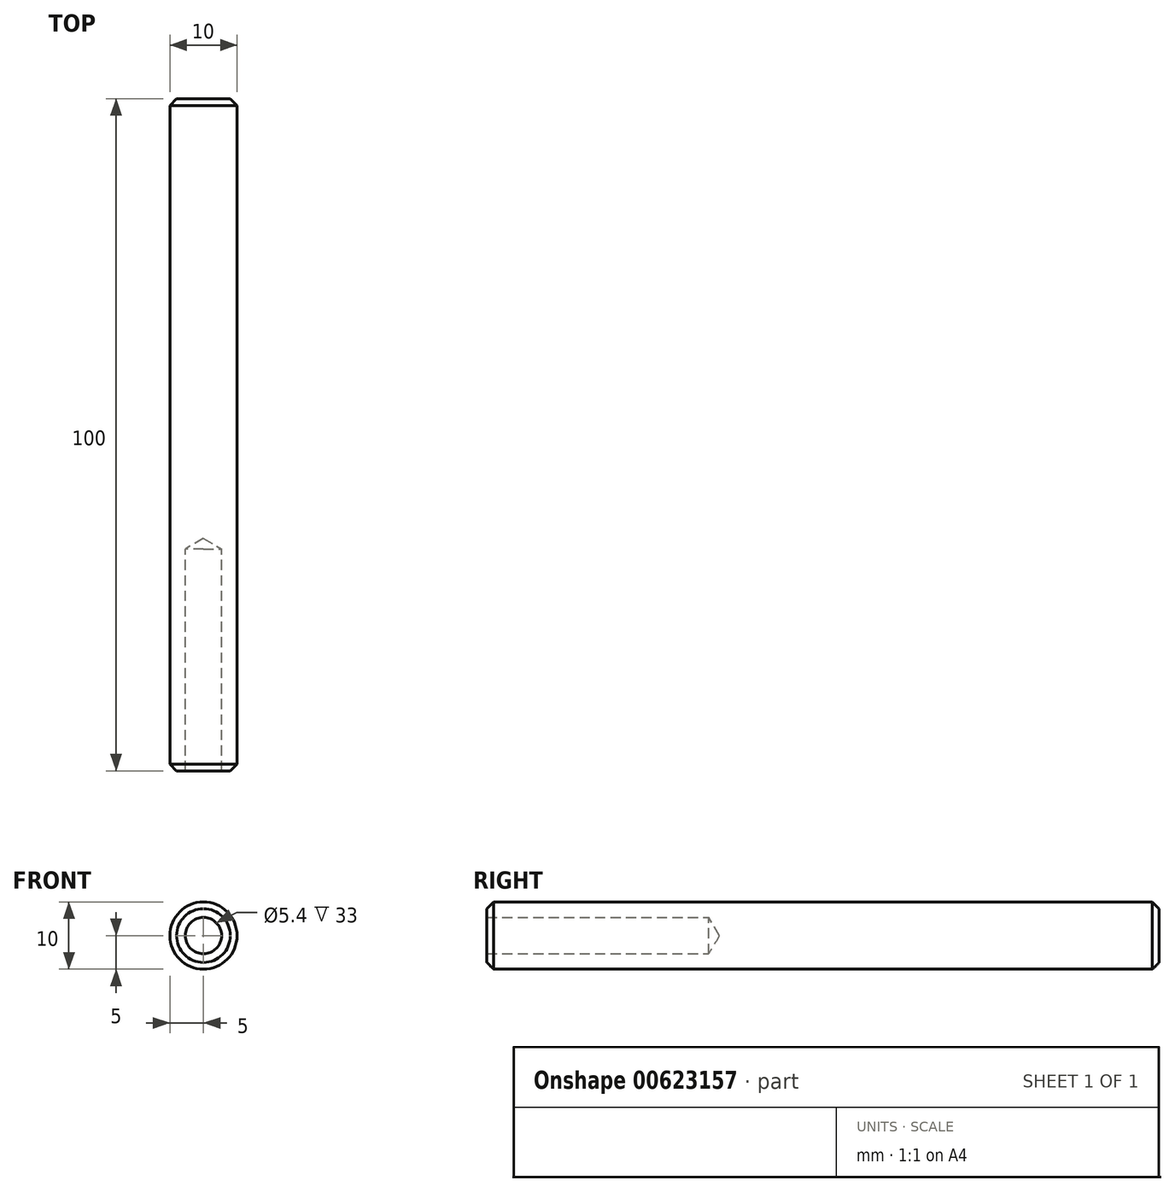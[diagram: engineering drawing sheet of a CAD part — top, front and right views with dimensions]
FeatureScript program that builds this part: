
annotation { "Feature Type Name" : "Feature", "Feature Type Description" : "" }
export const myFeature = defineFeature(function(context is Context, id is Id, definition is map)
    precondition{}
    {
        {
            var Q0;
            Q0=qCreatedBy(makeId("Front.planeOp"),FACE);
            var sketch = newSketch(context, id + "F0", { "sketchPlane" : qUnion([Q0])});
            skCircle(sketch, "E0", {"center": v(0, 0) * mm, "radius": 5 * mm});
            skSolve(sketch);
        }
        {
            var Q0;
            Q0=qSketchRegion(id+"F0",true);
            extrude(context, id + "F1", {"entities" : qUnion([Q0]), "offsetDistance" : 25 * mm, "depth" : 100 * mm});
        }
        {
            var Q0;
            Q0=makeQuery(id+"F1.opExtrude","CAP_EDGE",EDGE,{"disambiguationData":[OSD([sQuery(id+"F0.wireOp",EDGE,"E0")])],"isStart":false});
            var Q1;
            Q1=makeQuery(id+"F1.opExtrude","CAP_EDGE",EDGE,{"disambiguationData":[OSD([sQuery(id+"F0.wireOp",EDGE,"E0")])],"isStart":true});
            chamfer(context, id + "F2", {"entities" : qUnion([Q0, Q1]), "width" : 1 * mm, "tangentPropagation" : true});
        }
        {
            var Q0;
            Q0=makeQuery(id+"F1.opExtrude","CAP_FACE",FACE,{"disambiguationData":[OSD([sQuery(id+"F0.wireOp",EDGE,"E0")])],"isStart":false});
            var sketch = newSketch(context, id + "F3", { "sketchPlane" : qUnion([Q0])});
            skPoint(sketch, "E1", {"position": v(0, 0) * mm});
            skSolve(sketch);
        }
        {
            var Q0;
            Q0=sQuery(id+"F3.wireOp",VERTEX,"E1");
            var Q1;
            Q1=makeQuery(id+"F1.opExtrude","SWEPT_BODY",BODY,{"disambiguationData":[OSD([sQuery(id+"F0.wireOp",EDGE,"E0")])]});
            hole(context, id + "F4", {"style" : HoleStyle.SIMPLE, "endStyle" : HoleEndStyle.BLIND, "standardTappedOrClearance" : lookupTablePath({ "standard" : "ISO", "engagement" : "50%", "pitch" : "1 mm", "size" : "M6", "type" : "Tapped" }), "standardBlindInLast" : lookupTablePath({ "standard" : "ISO", "fit" : "Normal", "engagement" : "50%", "pitch" : "1 mm", "size" : "M6", "type" : "Clearance & tapped" }), "holeDiameter" : 5.4 * mm, "majorDiameter" : 6 * mm, "showTappedDepth" : true, "holeDepth" : 33 * mm, "isTappedThrough" : true, "tappedDepth" : 30 * mm, "tapClearance" : 3, "locations" : qUnion([Q0]), "scope" : qUnion([Q1])});
        }
    });
